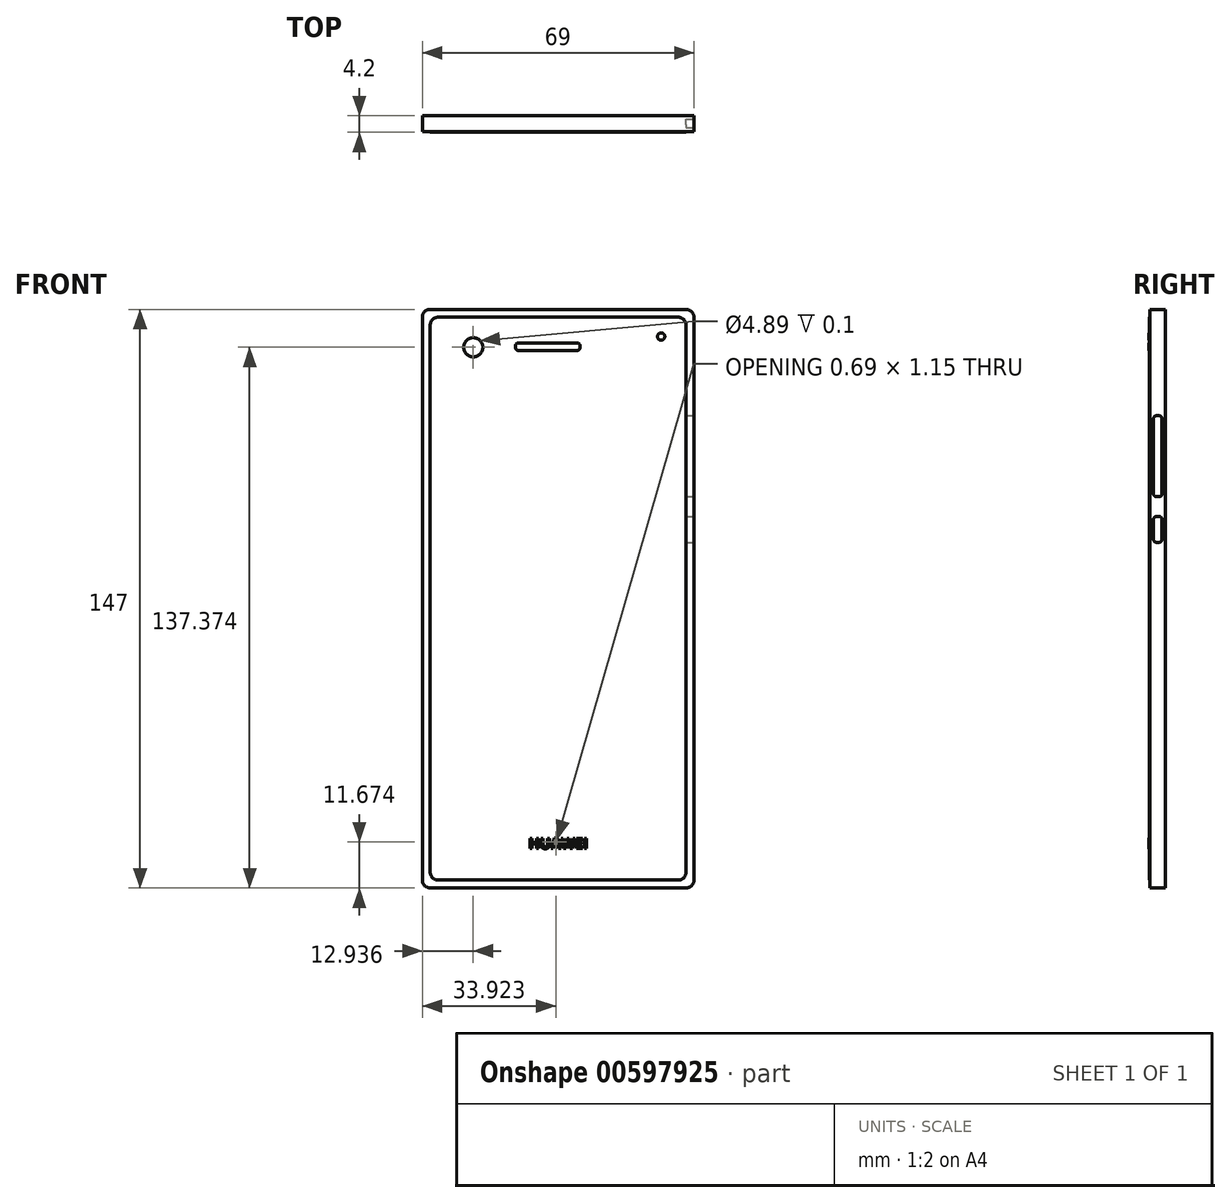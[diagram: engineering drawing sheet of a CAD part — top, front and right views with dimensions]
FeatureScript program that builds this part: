
annotation { "Feature Type Name" : "Feature", "Feature Type Description" : "" }
export const myFeature = defineFeature(function(context is Context, id is Id, definition is map)
    precondition{}
    {
        {
            var Q0;
            Q0=qCreatedBy(makeId("Front.planeOp"),FACE);
            var sketch = newSketch(context, id + "F0", { "sketchPlane" : qUnion([Q0])});
            skLineSegment(sketch, "E0", {"start": v(0, 2) * mm, "end": v(0, 145) * mm});
            skLineSegment(sketch, "E1", {"start": v(-2, 147) * mm, "end": v(-67, 147) * mm});
            skLineSegment(sketch, "E2", {"start": v(-69, 145) * mm, "end": v(-69, 2) * mm});
            skLineSegment(sketch, "E3", {"start": v(-67, 0) * mm, "end": v(-2, 0) * mm});
            skPoint(sketch, "E4.visualSharp", {"position": v(-69, 147) * mm});
            skArc(sketch, "E4.filletArc", {"start": v(-67, 147) * mm, "mid": v(-68.41, 146.41) * mm, "end": v(-69, 145) * mm});
            skPoint(sketch, "E5.visualSharp", {"position": v(0, 147) * mm});
            skArc(sketch, "E5.filletArc", {"start": v(0, 145) * mm, "mid": v(-0.59, 146.41) * mm, "end": v(-2, 147) * mm});
            skPoint(sketch, "E6.visualSharp", {"position": v(0, 0) * mm});
            skArc(sketch, "E6.filletArc", {"start": v(-2, 0) * mm, "mid": v(-0.59, 0.59) * mm, "end": v(0, 2) * mm});
            skPoint(sketch, "E7.visualSharp", {"position": v(-69, 0) * mm});
            skArc(sketch, "E7.filletArc", {"start": v(-69, 2) * mm, "mid": v(-68.41, 0.59) * mm, "end": v(-67, 0) * mm});
            skSolve(sketch);
        }
        {
            var Q0;
            Q0=makeQuery(id+"F0.imprint","IMPRINT",FACE,{"disambiguationData":[TD([[makeQuery(id+"F0.imprint","IMPRINT",EDGE,{"derivedFrom":sQuery(id+"F0.wireOp",EDGE,"E0")}),1.0]])]});
            extrude(context, id + "F1", {"entities" : qUnion([Q0]), "depth" : 4 * mm, "offsetDistance" : 25 * mm});
        }
        {
            var Q0;
            Q0=makeQuery(id+"F1.opExtrude","SWEPT_FACE",FACE,{"disambiguationData":[OSD([sQuery(id+"F0.wireOp",EDGE,"E0")])]});
            var sketch = newSketch(context, id + "F2", { "sketchPlane" : qUnion([Q0])});
            skLineSegment(sketch, "E8.bottom", {"start": v(-2.25, 120) * mm, "end": v(-1.65, 120) * mm});
            skLineSegment(sketch, "E8.top", {"start": v(-2.25, 99.4) * mm, "end": v(-1.65, 99.4) * mm});
            skLineSegment(sketch, "E8.left", {"start": v(-3.05, 119.2) * mm, "end": v(-3.05, 100.2) * mm});
            skLineSegment(sketch, "E8.right", {"start": v(-0.85, 119.2) * mm, "end": v(-0.85, 100.2) * mm});
            skPoint(sketch, "E9.visualSharp", {"position": v(-3.05, 120) * mm});
            skArc(sketch, "E9.filletArc", {"start": v(-2.25, 120) * mm, "mid": v(-2.82, 119.77) * mm, "end": v(-3.05, 119.2) * mm});
            skPoint(sketch, "E10.visualSharp", {"position": v(-0.85, 120) * mm});
            skArc(sketch, "E10.filletArc", {"start": v(-0.85, 119.2) * mm, "mid": v(-1.09, 119.77) * mm, "end": v(-1.65, 120) * mm});
            skPoint(sketch, "E11.visualSharp", {"position": v(-3.05, 99.4) * mm});
            skArc(sketch, "E11.filletArc", {"start": v(-3.05, 100.2) * mm, "mid": v(-2.82, 99.63) * mm, "end": v(-2.25, 99.4) * mm});
            skPoint(sketch, "E12.visualSharp", {"position": v(-0.85, 99.4) * mm});
            skArc(sketch, "E12.filletArc", {"start": v(-1.65, 99.4) * mm, "mid": v(-1.09, 99.63) * mm, "end": v(-0.85, 100.2) * mm});
            skPoint(sketch, "E13.visualSharp", {"position": v(-0.85, 104.4) * mm});
            skPoint(sketch, "E14.visualSharp", {"position": v(-3.1, 104.4) * mm});
            skLineSegment(sketch, "E15.bottom", {"start": v(-2.25, 94.4) * mm, "end": v(-1.65, 94.4) * mm});
            skLineSegment(sketch, "E15.top", {"start": v(-2.25, 87.8) * mm, "end": v(-1.65, 87.8) * mm});
            skLineSegment(sketch, "E15.left", {"start": v(-3.05, 93.6) * mm, "end": v(-3.05, 88.6) * mm});
            skLineSegment(sketch, "E15.right", {"start": v(-0.85, 93.6) * mm, "end": v(-0.85, 88.6) * mm});
            skPoint(sketch, "E16.visualSharp", {"position": v(-3.05, 94.4) * mm});
            skArc(sketch, "E16.filletArc", {"start": v(-2.25, 94.4) * mm, "mid": v(-2.82, 94.17) * mm, "end": v(-3.05, 93.6) * mm});
            skPoint(sketch, "E17.visualSharp", {"position": v(-0.85, 94.4) * mm});
            skArc(sketch, "E17.filletArc", {"start": v(-0.85, 93.6) * mm, "mid": v(-1.09, 94.17) * mm, "end": v(-1.65, 94.4) * mm});
            skPoint(sketch, "E18.visualSharp", {"position": v(-3.05, 87.8) * mm});
            skArc(sketch, "E18.filletArc", {"start": v(-3.05, 88.6) * mm, "mid": v(-2.82, 88.03) * mm, "end": v(-2.25, 87.8) * mm});
            skPoint(sketch, "E19.visualSharp", {"position": v(-0.85, 87.8) * mm});
            skArc(sketch, "E19.filletArc", {"start": v(-1.65, 87.8) * mm, "mid": v(-1.09, 88.03) * mm, "end": v(-0.85, 88.6) * mm});
            skSolve(sketch);
        }
        {
            var Q0;
            Q0 = qSketchRegion(id + "F2", true);
            extrude(context, id + "F3", {"entities" : qUnion([Q0]), "operationType" : NewBodyOperationType.REMOVE, "oppositeDirection" : true, "depth" : 2 * mm, "offsetDistance" : 25 * mm});
        }
        {
            var Q0;
            Q0=makeQuery(id+"F1.opExtrude","CAP_FACE",FACE,{"disambiguationData":[OSD([sQuery(id+"F0.wireOp",EDGE,"E0"),sQuery(id+"F0.wireOp",EDGE,"E1"),sQuery(id+"F0.wireOp",EDGE,"E2"),sQuery(id+"F0.wireOp",EDGE,"E3"),sQuery(id+"F0.wireOp",EDGE,"E4.filletArc"),sQuery(id+"F0.wireOp",EDGE,"E5.filletArc"),sQuery(id+"F0.wireOp",EDGE,"E6.filletArc"),sQuery(id+"F0.wireOp",EDGE,"E7.filletArc")])],"isStart":false});
            var sketch = newSketch(context, id + "F4", { "sketchPlane" : qUnion([Q0])});
            skLineSegment(sketch, "E20", {"start": v(-65, 145) * mm, "end": v(-4, 145) * mm});
            skLineSegment(sketch, "E21", {"start": v(-2, 143) * mm, "end": v(-2, 4) * mm});
            skLineSegment(sketch, "E22", {"start": v(-4, 2) * mm, "end": v(-65, 2) * mm});
            skLineSegment(sketch, "E23", {"start": v(-67, 4) * mm, "end": v(-67, 143) * mm});
            skPoint(sketch, "E24.visualSharp", {"position": v(-67, 145) * mm});
            skArc(sketch, "E24.filletArc", {"start": v(-65, 145) * mm, "mid": v(-66.41, 144.41) * mm, "end": v(-67, 143) * mm});
            skPoint(sketch, "E25.visualSharp", {"position": v(-2, 145) * mm});
            skArc(sketch, "E25.filletArc", {"start": v(-2, 143) * mm, "mid": v(-2.59, 144.41) * mm, "end": v(-4, 145) * mm});
            skPoint(sketch, "E26.visualSharp", {"position": v(-2, 2) * mm});
            skArc(sketch, "E26.filletArc", {"start": v(-4, 2) * mm, "mid": v(-2.59, 2.59) * mm, "end": v(-2, 4) * mm});
            skPoint(sketch, "E27.visualSharp", {"position": v(-67, 2) * mm});
            skArc(sketch, "E27.filletArc", {"start": v(-67, 4) * mm, "mid": v(-66.41, 2.59) * mm, "end": v(-65, 2) * mm});
            skSolve(sketch);
        }
        {
            var Q0;
            Q0 = qSketchRegion(id + "F4", true);
            extrude(context, id + "F5", {"entities" : qUnion([Q0]), "depth" : 0.1 * mm, "offsetDistance" : 25 * mm});
        }
        {
            var Q0;
            Q0=makeQuery(id+"F1.opExtrude","CAP_FACE",FACE,{"disambiguationData":[OSD([sQuery(id+"F0.wireOp",EDGE,"E0"),sQuery(id+"F0.wireOp",EDGE,"E1"),sQuery(id+"F0.wireOp",EDGE,"E2"),sQuery(id+"F0.wireOp",EDGE,"E3"),sQuery(id+"F0.wireOp",EDGE,"E4.filletArc"),sQuery(id+"F0.wireOp",EDGE,"E5.filletArc"),sQuery(id+"F0.wireOp",EDGE,"E6.filletArc"),sQuery(id+"F0.wireOp",EDGE,"E7.filletArc")])],"isStart":false});
            var sketch = newSketch(context, id + "F6", { "sketchPlane" : qUnion([Q0])});
            skLineSegment(sketch, "E28.bottom", {"start": v(-66.9, 131) * mm, "end": v(-2.1, 131) * mm});
            skLineSegment(sketch, "E28.top", {"start": v(-66.9, 20) * mm, "end": v(-2.1, 20) * mm});
            skLineSegment(sketch, "E28.left", {"start": v(-66.9, 131) * mm, "end": v(-66.9, 20) * mm});
            skLineSegment(sketch, "E28.right", {"start": v(-2.1, 131) * mm, "end": v(-2.1, 20) * mm});
            skPoint(sketch, "E29.centerSnap0", {"position": v(-34.42, 137.88) * mm});
            skPoint(sketch, "E30.visualSharp", {"position": v(-44.46, 137.88) * mm});
            skPoint(sketch, "E31.visualSharp", {"position": v(-44.46, 136.39) * mm});
            skSolve(sketch);
        }
        {
            var Q0;
            Q0=makeQuery(id+"F6.imprint","IMPRINT",FACE,{"disambiguationData":[TD([[makeQuery(id+"F6.imprint","IMPRINT",EDGE,{"derivedFrom":sQuery(id+"F6.wireOp",EDGE,"E28.bottom")}),-1.0]])]});
            extrude(context, id + "F7", {"entities" : qUnion([Q0]), "operationType" : NewBodyOperationType.ADD, "depth" : 0.1 * mm, "offsetDistance" : 25 * mm});
        }
        {
            var Q0;
            Q0=makeQuery(id+"F5.opExtrude","CAP_FACE",FACE,{"disambiguationData":[OSD([sQuery(id+"F4.wireOp",EDGE,"E20"),sQuery(id+"F4.wireOp",EDGE,"E21"),sQuery(id+"F4.wireOp",EDGE,"E22"),sQuery(id+"F4.wireOp",EDGE,"E23"),sQuery(id+"F4.wireOp",EDGE,"E24.filletArc"),sQuery(id+"F4.wireOp",EDGE,"E25.filletArc"),sQuery(id+"F4.wireOp",EDGE,"E26.filletArc"),sQuery(id+"F4.wireOp",EDGE,"E27.filletArc")])],"isStart":false});
            var sketch = newSketch(context, id + "F8", { "sketchPlane" : qUnion([Q0])});
            skLineSegment(sketch, "E32.bottom", {"start": v(-44.64, 138.48) * mm, "end": v(-29.64, 138.48) * mm});
            skLineSegment(sketch, "E32.top", {"start": v(-44.64, 136.58) * mm, "end": v(-29.64, 136.58) * mm});
            skLineSegment(sketch, "E32.left", {"start": v(-45.34, 137.78) * mm, "end": v(-45.34, 137.28) * mm});
            skLineSegment(sketch, "E32.right", {"start": v(-28.94, 137.78) * mm, "end": v(-28.94, 137.28) * mm});
            skPoint(sketch, "E33.visualSharp", {"position": v(-45.34, 138.48) * mm});
            skArc(sketch, "E33.filletArc", {"start": v(-44.64, 138.48) * mm, "mid": v(-45.13, 138.28) * mm, "end": v(-45.34, 137.78) * mm});
            skPoint(sketch, "E34.visualSharp", {"position": v(-45.34, 136.58) * mm});
            skArc(sketch, "E34.filletArc", {"start": v(-45.34, 137.28) * mm, "mid": v(-45.13, 136.79) * mm, "end": v(-44.64, 136.58) * mm});
            skPoint(sketch, "E35.visualSharp", {"position": v(-28.94, 138.48) * mm});
            skArc(sketch, "E35.filletArc", {"start": v(-28.94, 137.78) * mm, "mid": v(-29.14, 138.28) * mm, "end": v(-29.64, 138.48) * mm});
            skPoint(sketch, "E36.visualSharp", {"position": v(-28.94, 136.58) * mm});
            skArc(sketch, "E36.filletArc", {"start": v(-29.64, 136.58) * mm, "mid": v(-29.14, 136.79) * mm, "end": v(-28.94, 137.28) * mm});
            skSolve(sketch);
        }
        {
            var Q0;
            Q0 = qSketchRegion(id + "F8", true);
            extrude(context, id + "F9", {"entities" : qUnion([Q0]), "depth" : 0.1 * mm, "offsetDistance" : 25 * mm});
        }
        {
            var Q0;
            Q0=makeQuery(id+"F5.opExtrude","CAP_FACE",FACE,{"disambiguationData":[OSD([sQuery(id+"F4.wireOp",EDGE,"E20"),sQuery(id+"F4.wireOp",EDGE,"E21"),sQuery(id+"F4.wireOp",EDGE,"E22"),sQuery(id+"F4.wireOp",EDGE,"E23"),sQuery(id+"F4.wireOp",EDGE,"E24.filletArc"),sQuery(id+"F4.wireOp",EDGE,"E25.filletArc"),sQuery(id+"F4.wireOp",EDGE,"E26.filletArc"),sQuery(id+"F4.wireOp",EDGE,"E27.filletArc")])],"isStart":false});
            var sketch = newSketch(context, id + "F10", { "sketchPlane" : qUnion([Q0])});
            skCircle(sketch, "E37", {"center": v(-56.06, 137.37) * mm, "radius": 2.45 * mm});
            skSolve(sketch);
        }
        {
            var Q0;
            Q0 = qSketchRegion(id + "F10", true);
            extrude(context, id + "F11", {"entities" : qUnion([Q0]), "operationType" : NewBodyOperationType.REMOVE, "oppositeDirection" : true, "depth" : 0.1 * mm, "offsetDistance" : 25 * mm});
        }
        {
            var Q0;
            Q0=makeQuery(id+"F5.opExtrude","CAP_FACE",FACE,{"disambiguationData":[OSD([sQuery(id+"F4.wireOp",EDGE,"E20"),sQuery(id+"F4.wireOp",EDGE,"E21"),sQuery(id+"F4.wireOp",EDGE,"E22"),sQuery(id+"F4.wireOp",EDGE,"E23"),sQuery(id+"F4.wireOp",EDGE,"E24.filletArc"),sQuery(id+"F4.wireOp",EDGE,"E25.filletArc"),sQuery(id+"F4.wireOp",EDGE,"E26.filletArc"),sQuery(id+"F4.wireOp",EDGE,"E27.filletArc")])],"isStart":false});
            var sketch = newSketch(context, id + "F12", { "sketchPlane" : qUnion([Q0])});
            skCircle(sketch, "E38", {"center": v(-8.33, 140.1) * mm, "radius": 0.93 * mm});
            skSolve(sketch);
        }
        {
            var Q0;
            Q0 = qSketchRegion(id + "F12", true);
            extrude(context, id + "F13", {"entities" : qUnion([Q0]), "depth" : 0.1 * mm, "offsetDistance" : 25 * mm});
        }
        {
            var Q0;
            Q0=makeQuery(id+"F5.opExtrude","CAP_FACE",FACE,{"disambiguationData":[OSD([sQuery(id+"F4.wireOp",EDGE,"E20"),sQuery(id+"F4.wireOp",EDGE,"E21"),sQuery(id+"F4.wireOp",EDGE,"E22"),sQuery(id+"F4.wireOp",EDGE,"E23"),sQuery(id+"F4.wireOp",EDGE,"E24.filletArc"),sQuery(id+"F4.wireOp",EDGE,"E25.filletArc"),sQuery(id+"F4.wireOp",EDGE,"E26.filletArc"),sQuery(id+"F4.wireOp",EDGE,"E27.filletArc")])],"isStart":false});
            var sketch = newSketch(context, id + "F14", { "sketchPlane" : qUnion([Q0])});
            skText(sketch, "E39", { "text": "HUAWEI", "fontName": "OpenSans-Bold.ttf"});
            const initialGuessF14  = {"E39": [-0.042, 0.01, 1, 0, 0.00267]};
            skSetInitialGuess(sketch, initialGuessF14);
            skSolve(sketch);
        }
        {
            var Q0;
            Q0 = qSketchRegion(id + "F14", true);
            extrude(context, id + "F15", {"entities" : qUnion([Q0]), "depth" : 0.1 * mm, "offsetDistance" : 25 * mm});
        }
    });
